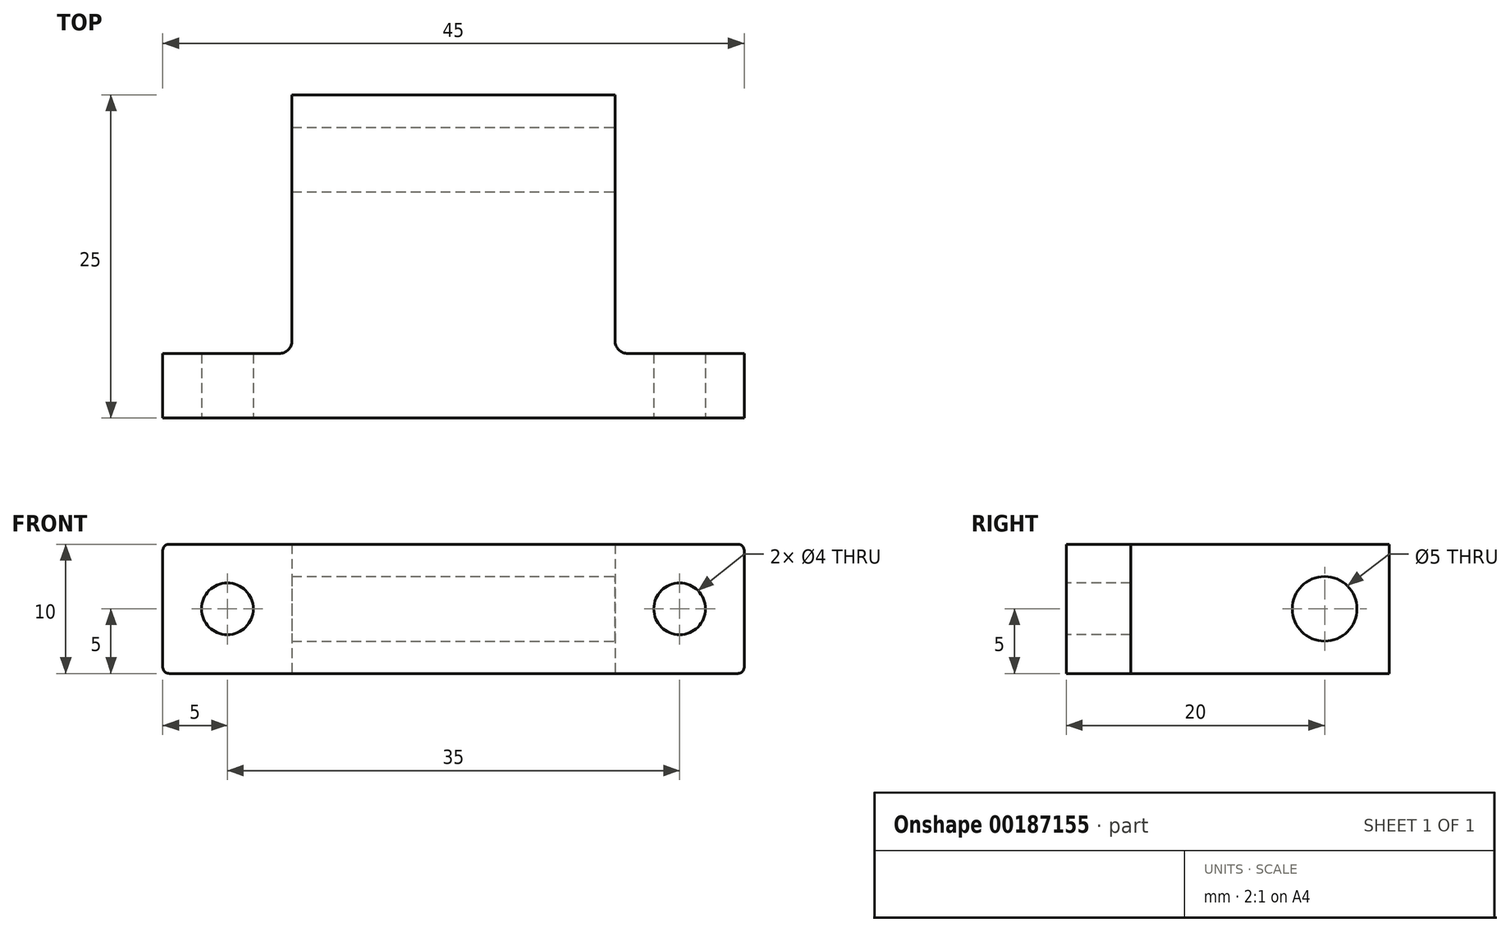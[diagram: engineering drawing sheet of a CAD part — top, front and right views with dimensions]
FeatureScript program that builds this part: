
annotation { "Feature Type Name" : "Feature", "Feature Type Description" : "" }
export const myFeature = defineFeature(function(context is Context, id is Id, definition is map)
    precondition{}
    {
        {
            var Q0;
            Q0=qCreatedBy(makeId("Top.planeOp"),FACE);
            var sketch = newSketch(context, id + "F0", { "sketchPlane" : qUnion([Q0])});
            skLineSegment(sketch, "E0", {"start": v(0, 0) * mm, "end": v(0, 5) * mm});
            skLineSegment(sketch, "E1", {"start": v(0, 5) * mm, "end": v(10, 5) * mm});
            skLineSegment(sketch, "E2", {"start": v(10, 5) * mm, "end": v(10, 25) * mm});
            skLineSegment(sketch, "E3", {"start": v(10, 25) * mm, "end": v(35, 25) * mm});
            skLineSegment(sketch, "E4", {"start": v(35, 25) * mm, "end": v(35, 5) * mm});
            skLineSegment(sketch, "E5", {"start": v(35, 5) * mm, "end": v(45, 5) * mm});
            skLineSegment(sketch, "E6", {"start": v(45, 5) * mm, "end": v(45, 0) * mm});
            skLineSegment(sketch, "E7", {"start": v(45, 0) * mm, "end": v(0, 0) * mm});
            skSolve(sketch);
        }
        {
            var Q0;
            Q0=makeQuery(id+"F0.imprint","IMPRINT",FACE,{"disambiguationData":[TD([[makeQuery(id+"F0.imprint","IMPRINT",EDGE,{"derivedFrom":sQuery(id+"F0.wireOp",EDGE,"E0")}),-1.0]])]});
            extrude(context, id + "F1", {"entities" : qUnion([Q0]), "depth" : 10 * mm});
        }
        {
            var Q0;
            Q0=makeQuery(id+"F1.opExtrude","SWEPT_FACE",FACE,{"disambiguationData":[OSD([sQuery(id+"F0.wireOp",EDGE,"E4")])]});
            var sketch = newSketch(context, id + "F2", { "sketchPlane" : qUnion([Q0])});
            skLineSegment(sketch, "E8", {"start": v(25, 5) * mm, "end": v(20, 5) * mm, "construction": true});
            skPoint(sketch, "E9", {"position": v(20, 5) * mm});
            skSolve(sketch);
        }
        {
            var Q0;
            Q0=sQuery(id+"F2.wireOp",VERTEX,"E9");
            var Q1;
            Q1=makeQuery(id+"F1.opExtrude","SWEPT_BODY",BODY,{"disambiguationData":[OSD([sQuery(id+"F0.wireOp",EDGE,"E0"),sQuery(id+"F0.wireOp",EDGE,"E1"),sQuery(id+"F0.wireOp",EDGE,"E2"),sQuery(id+"F0.wireOp",EDGE,"E3"),sQuery(id+"F0.wireOp",EDGE,"E4"),sQuery(id+"F0.wireOp",EDGE,"E5"),sQuery(id+"F0.wireOp",EDGE,"E6"),sQuery(id+"F0.wireOp",EDGE,"E7")])]});
            hole(context, id + "F3", {"style" : HoleStyle.SIMPLE, "endStyle" : HoleEndStyle.THROUGH, "holeDiameter" : 5 * mm, "locations" : qUnion([Q0]), "scope" : qUnion([Q1]), "isTappedThrough" : true});
        }
        {
            var Q0;
            Q0=makeQuery(id+"F1.opExtrude","SWEPT_FACE",FACE,{"disambiguationData":[OSD([sQuery(id+"F0.wireOp",EDGE,"E7")])]});
            var sketch = newSketch(context, id + "F4", { "sketchPlane" : qUnion([Q0])});
            skLineSegment(sketch, "E10", {"start": v(0, 5) * mm, "end": v(5, 5) * mm, "construction": true});
            skLineSegment(sketch, "E11", {"start": v(5, 5) * mm, "end": v(40, 5) * mm, "construction": true});
            skLineSegment(sketch, "E12", {"start": v(40, 5) * mm, "end": v(45, 5) * mm, "construction": true});
            skPoint(sketch, "E13", {"position": v(5, 5) * mm});
            skPoint(sketch, "E14", {"position": v(40, 5) * mm});
            skSolve(sketch);
        }
        {
            var Q0;
            Q0=sQuery(id+"F4.wireOp",VERTEX,"E13");
            var Q1;
            Q1=sQuery(id+"F4.wireOp",VERTEX,"E14");
            var Q2;
            Q2=makeQuery(id+"F1.opExtrude","SWEPT_BODY",BODY,{"disambiguationData":[OSD([sQuery(id+"F0.wireOp",EDGE,"E0"),sQuery(id+"F0.wireOp",EDGE,"E1"),sQuery(id+"F0.wireOp",EDGE,"E2"),sQuery(id+"F0.wireOp",EDGE,"E3"),sQuery(id+"F0.wireOp",EDGE,"E4"),sQuery(id+"F0.wireOp",EDGE,"E5"),sQuery(id+"F0.wireOp",EDGE,"E6"),sQuery(id+"F0.wireOp",EDGE,"E7")])]});
            hole(context, id + "F5", {"style" : HoleStyle.SIMPLE, "endStyle" : HoleEndStyle.THROUGH, "holeDiameter" : 4 * mm, "locations" : qUnion([Q0, Q1]), "scope" : qUnion([Q2]), "isTappedThrough" : true});
        }
        {
            var Q0;
            Q0=makeQuery(id+"F1.opExtrude","CAP_EDGE",EDGE,{"disambiguationData":[OSD([sQuery(id+"F0.wireOp",EDGE,"E0")])],"isStart":false});
            var Q1;
            Q1=makeQuery(id+"F1.opExtrude","CAP_EDGE",EDGE,{"disambiguationData":[OSD([sQuery(id+"F0.wireOp",EDGE,"E0")])],"isStart":true});
            var Q2;
            Q2=makeQuery(id+"F1.opExtrude","CAP_EDGE",EDGE,{"disambiguationData":[OSD([sQuery(id+"F0.wireOp",EDGE,"E6")])],"isStart":false});
            var Q3;
            Q3=makeQuery(id+"F1.opExtrude","CAP_EDGE",EDGE,{"disambiguationData":[OSD([sQuery(id+"F0.wireOp",EDGE,"E6")])],"isStart":true});
            fillet(context, id + "F6", {"entities" : qUnion([Q0, Q1, Q2, Q3]), "radius" : 0.5 * mm, "tangentPropagation" : true, "allowEdgeOverflow" : false});
        }
        {
            var Q0;
            Q0=makeQuery(id+"F1.opExtrude","SWEPT_EDGE",EDGE,{"disambiguationData":[OSD([sQuery(id+"F0.wireOp",EDGE,"E1"),sQuery(id+"F0.wireOp",EDGE,"E2")])]});
            var Q1;
            Q1=makeQuery(id+"F1.opExtrude","SWEPT_EDGE",EDGE,{"disambiguationData":[OSD([sQuery(id+"F0.wireOp",EDGE,"E4"),sQuery(id+"F0.wireOp",EDGE,"E5")])]});
            fillet(context, id + "F7", {"entities" : qUnion([Q0, Q1]), "radius" : 1 * mm, "tangentPropagation" : true, "allowEdgeOverflow" : false});
        }
    });
